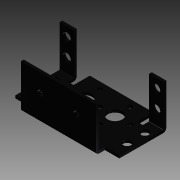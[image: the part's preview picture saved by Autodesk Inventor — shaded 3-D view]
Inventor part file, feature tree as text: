
AUTODESK INVENTOR PART (.ipt)
format: ipt  version: 2015 (Build 190159000, 159)  size: 181,248 bytes
history: native  units: in
note: dims shown in document units (in); Inventor stores cm internally (conversion verified against a paired STEP export)
features: fillet x1, other x1, sketch x1, imported_body x1
ambient origin geometry x8: Origin, YZ Plane, XZ Plane, XY Plane, X Axis, Y Axis, Z Axis, Center Point
bodies: Body1 (feature_tree)
feature tree (4):
  fillet  "Fillet5"  Radius=0.782in
  other  "asb-041"
  sketch  "Sketch1"  dims[d1=2.25in]
  imported_body  "Base1"
